# Revit family: check valve 2621 00 (01)
name_source: partatom
category: Rohrzubehör
revit_build: Autodesk Revit 2018 (Build: 20190510_1515(x64)
units: mm (PartAtom-declared; Revit-internal decimal feet)

## family parameters
Arbeitsebenenbasiert = Nein
Beim Laden mit Abzugskörper schneiden = Nein
Bemaßung runder Anschluss = Durchmesser verwenden
Gemeinsam genutzt = Nein
Immer vertikal = Ja
OmniClass-Nummer = 23.65.55.14
OmniClass-Titel = Valves for Liquid Services
Teiletyp = Normal

## types (1)
- check valve 2621 00 (01)
    H01 = 9.5 mm  [stored 0.031168 ft]
    H03 = 9.5 mm  [stored 0.031168 ft]
    Hersteller = Herz-Armaturen GmbH
    Medium = water purity in accordance with the ÖNORM H 5195 and VDI 2035 standards
    Nennweite IG = 10 mm  [stored 0.0328084 ft]
    SCRNCODE = 05;17;02
    SCRNSEQ = AWI;AWI_TYP="1007";2
    SCTWCODE = 04;14;02
    SCTWSEQ = FW;SBT_TYP_FW="108";2
    URL = www.herzvalves.com
    max. Operating pressure = 1000000.0 Pa
    max. Operating temperature = 110 °C

note: [stored X ft] marks values corroborated as IEEE doubles in the binary element streams (Revit-internal decimal feet)
